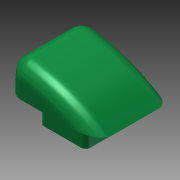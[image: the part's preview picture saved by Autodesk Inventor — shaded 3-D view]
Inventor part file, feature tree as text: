
AUTODESK INVENTOR PART (.ipt)
format: ipt  version: 2015 (Build 190159000, 159)  size: 292,864 bytes
history: native  units: in
note: dims shown in document units (in); Inventor stores cm internally (conversion verified against a paired STEP export)
features: extrude x3, sketch x3, fillet x2, shell x2
ambient origin geometry x8: Origin, YZ Plane, XZ Plane, XY Plane, X Axis, Y Axis, Z Axis, Center Point
bodies: Solid1 (feature_tree)
feature tree (10):
  extrude  "Extrusion1"  Depth=6.0in
  fillet  "Fillet1"  Radius=6.0in
  fillet  "Fillet2"  Radius=0.4in
  shell  "Shell1"  Thickness=0.64in
  extrude  "Extrusion2"  Depth=6.0in TaperAngle=0.0deg
  extrude  "Extrusion3"  Depth=0.15in
  shell  "Shell2"  Thickness=0.07in
  sketch  "Sketch1"  dims[d0=3.04in d4=3.01in d7=6.0in d8=0.4in d9=0.64in]
  sketch  "Sketch2"  dims[d10=6.0in d11=2.55in d12=0.0in]
  sketch  "Sketch3"  dims[d13=0.5in d14=0.5in d15=0.07in d16=0.68in d17=2.22in d18=2.26in d19=0.29in d20=0.15in d21=1.455in d22=0.0in d23=0.15in d24=0.29in d25=2.26in d26=2.22in d27=0.67in d28=0.0in d29=0.05in]
